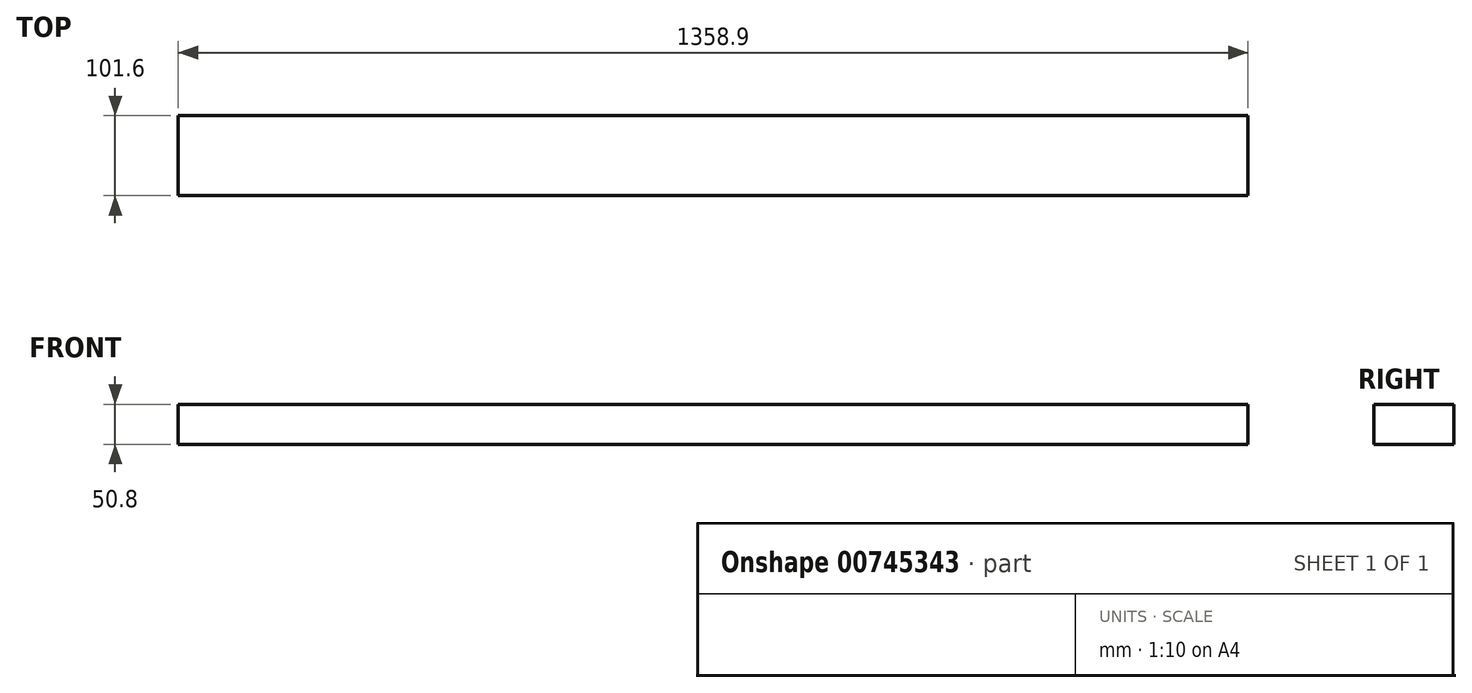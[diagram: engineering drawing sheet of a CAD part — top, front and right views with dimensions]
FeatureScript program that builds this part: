
annotation { "Feature Type Name" : "Feature", "Feature Type Description" : "" }
export const myFeature = defineFeature(function(context is Context, id is Id, definition is map)
    precondition{}
    {
        {
            var Q0;
            Q0=qCreatedBy(makeId("Top.planeOp"),FACE);
            var sketch = newSketch(context, id + "F0", { "sketchPlane" : qUnion([Q0])});
            skLineSegment(sketch, "E0.bottom", {"start": v(0, 0) * mm, "end": v(1358.9, 0) * mm});
            skLineSegment(sketch, "E0.top", {"start": v(0, 101.6) * mm, "end": v(1358.9, 101.6) * mm});
            skLineSegment(sketch, "E0.left", {"start": v(0, 0) * mm, "end": v(0, 101.6) * mm});
            skLineSegment(sketch, "E0.right", {"start": v(1358.9, 0) * mm, "end": v(1358.9, 101.6) * mm});
            skSolve(sketch);
        }
        {
            var Q0;
            Q0=makeQuery(id+"F0.imprint","IMPRINT",FACE,{"disambiguationData":[TD([[makeQuery(id+"F0.imprint","IMPRINT",EDGE,{"derivedFrom":sQuery(id+"F0.wireOp",EDGE,"E0.bottom")}),1.0]])]});
            extrude(context, id + "F1", {"entities" : qUnion([Q0]), "depth" : 50.8 * mm, "offsetDistance" : 25.4 * mm});
        }
    });
